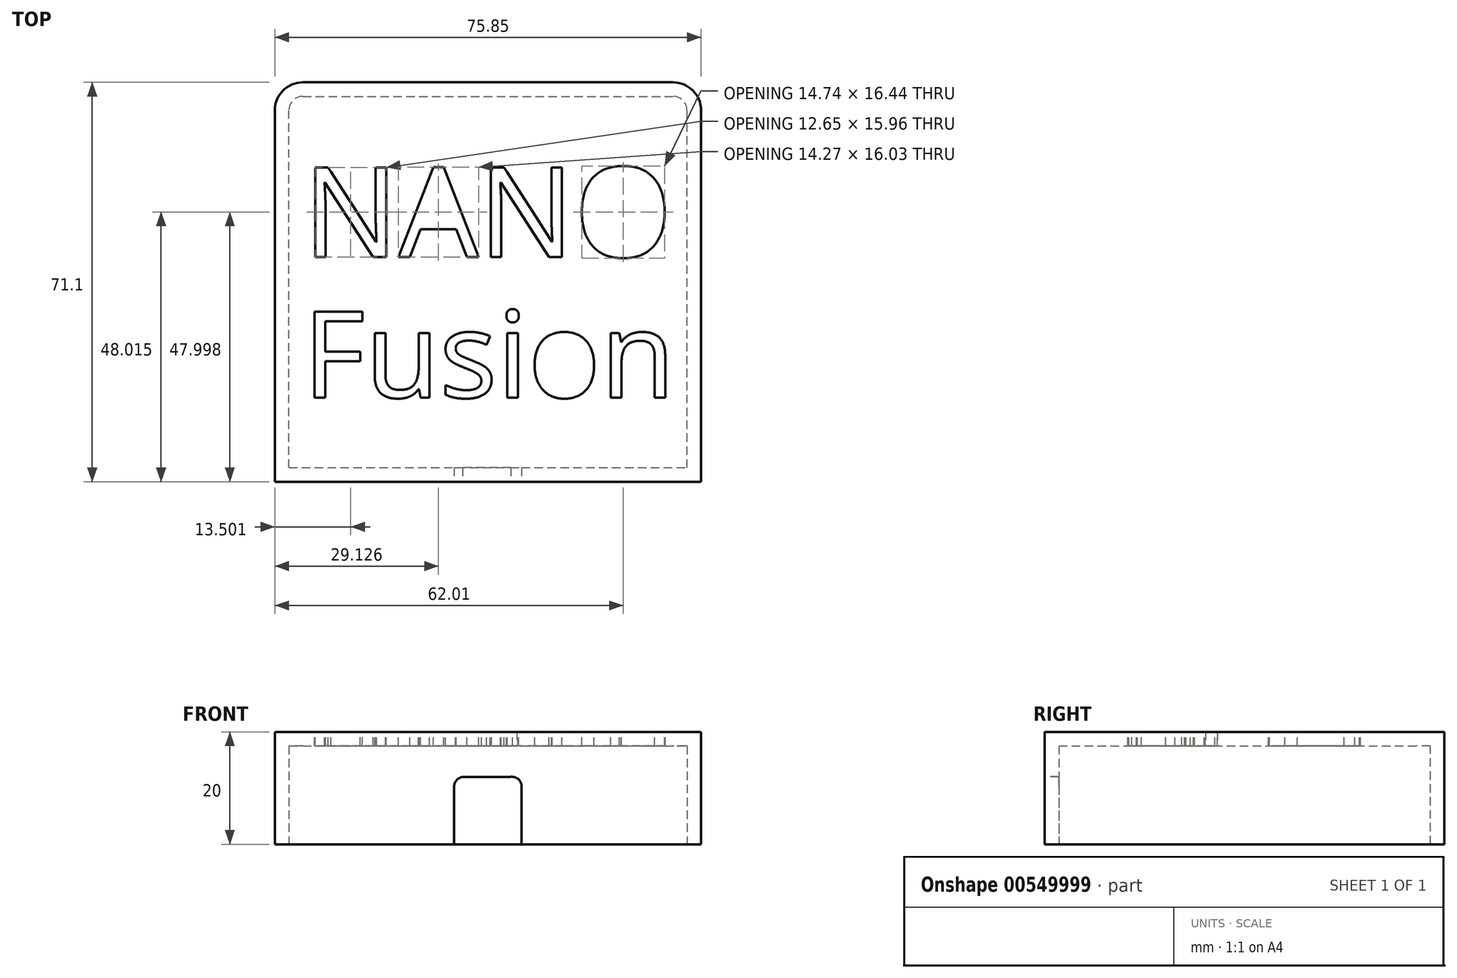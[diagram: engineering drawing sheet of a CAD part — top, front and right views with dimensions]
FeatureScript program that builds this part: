
annotation { "Feature Type Name" : "Feature", "Feature Type Description" : "" }
export const myFeature = defineFeature(function(context is Context, id is Id, definition is map)
    precondition{}
    {
        {
            var Q0;
            Q0=qCreatedBy(makeId("Top.planeOp"),FACE);
            var sketch = newSketch(context, id + "F0", { "sketchPlane" : qUnion([Q0])});
            skLineSegment(sketch, "E0.bottom", {"start": v(0, 0) * mm, "end": v(75.85, 0) * mm});
            skLineSegment(sketch, "E0.top", {"start": v(0, 66.1) * mm, "end": v(75.85, 66.1) * mm, "construction": true});
            skLineSegment(sketch, "E0.left", {"start": v(0, 0) * mm, "end": v(0, 66.1) * mm});
            skLineSegment(sketch, "E0.right", {"start": v(75.85, 0) * mm, "end": v(75.85, 66.1) * mm});
            skArc(sketch, "E1", {"start": v(0, 66.1) * mm, "mid": v(1.46, 69.64) * mm, "end": v(5, 71.1) * mm});
            skLineSegment(sketch, "E2", {"start": v(5, 71.1) * mm, "end": v(70.85, 71.1) * mm});
            skArc(sketch, "E3", {"start": v(70.85, 71.1) * mm, "mid": v(74.39, 69.64) * mm, "end": v(75.85, 66.1) * mm});
            skSolve(sketch);
        }
        {
            var Q0;
            Q0 = qSketchRegion(id + "F0", true);
            extrude(context, id + "F1", {"entities" : qUnion([Q0]), "depth" : 20 * mm, "offsetDistance" : 25 * mm});
        }
        {
            var Q0;
            Q0=makeQuery(id+"F1.opExtrude","CAP_FACE",FACE,{"disambiguationData":[OSD([sQuery(id+"F0.wireOp",EDGE,"E0.bottom"),sQuery(id+"F0.wireOp",EDGE,"E0.left"),sQuery(id+"F0.wireOp",EDGE,"E0.right"),sQuery(id+"F0.wireOp",EDGE,"E1"),sQuery(id+"F0.wireOp",EDGE,"E2"),sQuery(id+"F0.wireOp",EDGE,"E3")])],"isStart":true});
            shell(context, id + "F2", {"entities" : qUnion([Q0]), "thickness" : 2.5 * mm});
        }
        {
            var Q0;
            Q0=makeQuery(id+"F1.opExtrude","CAP_FACE",FACE,{"disambiguationData":[OSD([sQuery(id+"F0.wireOp",EDGE,"E0.bottom"),sQuery(id+"F0.wireOp",EDGE,"E0.left"),sQuery(id+"F0.wireOp",EDGE,"E0.right"),sQuery(id+"F0.wireOp",EDGE,"E1"),sQuery(id+"F0.wireOp",EDGE,"E2"),sQuery(id+"F0.wireOp",EDGE,"E3")])],"isStart":false});
            var sketch = newSketch(context, id + "F3", { "sketchPlane" : qUnion([Q0])});
            skText(sketch, "E4", { "text": "NANO", "fontName": "NotoSans-Regular.ttf"});
            skText(sketch, "E5", { "text": "Fusion", "fontName": "NotoSans-Regular.ttf"});
            const initialGuessF3  = {"E4": [0.005, 0.04, 1, 0, 0.0161], "E5": [0.005, 0.015, 1, 0, 0.01539]};
            skSetInitialGuess(sketch, initialGuessF3);
            skSolve(sketch);
        }
        {
            var Q0;
            Q0 = qSketchRegion(id + "F3", true);
            extrude(context, id + "F4", {"entities" : qUnion([Q0]), "operationType" : NewBodyOperationType.REMOVE, "oppositeDirection" : true, "depth" : 25 * mm, "offsetDistance" : 25 * mm});
        }
        {
            var Q0;
            Q0=makeQuery(id+"F4.boolean.opBoolean","SPLIT",FACE,{"disambiguationData":[TD([makeQuery(id+"F4.opExtrude","SWEPT_FACE",FACE,{"disambiguationData":[OSD([sQuery(id+"F3.wireOp",EDGE,"E4.sketch_text.stroke-26")])]})])],"derivedFrom":makeQuery(id+"F1.opExtrude","CAP_FACE",FACE,{"disambiguationData":[OSD([sQuery(id+"F0.wireOp",EDGE,"E0.bottom"),sQuery(id+"F0.wireOp",EDGE,"E0.left"),sQuery(id+"F0.wireOp",EDGE,"E0.right"),sQuery(id+"F0.wireOp",EDGE,"E1"),sQuery(id+"F0.wireOp",EDGE,"E2"),sQuery(id+"F0.wireOp",EDGE,"E3")])],"isStart":false})});
            extrude(context, id + "F5", {"entities" : qUnion([Q0]), "operationType" : NewBodyOperationType.REMOVE, "oppositeDirection" : true, "depth" : 25 * mm, "offsetDistance" : 25 * mm});
        }
        {
            var Q0;
            Q0=makeQuery(id+"F4.boolean.opBoolean","SPLIT",FACE,{"disambiguationData":[TD([makeQuery(id+"F4.opExtrude","SWEPT_FACE",FACE,{"disambiguationData":[OSD([sQuery(id+"F3.wireOp",EDGE,"E4.sketch_text.stroke-57")])]})])],"derivedFrom":makeQuery(id+"F1.opExtrude","CAP_FACE",FACE,{"disambiguationData":[OSD([sQuery(id+"F0.wireOp",EDGE,"E0.bottom"),sQuery(id+"F0.wireOp",EDGE,"E0.left"),sQuery(id+"F0.wireOp",EDGE,"E0.right"),sQuery(id+"F0.wireOp",EDGE,"E1"),sQuery(id+"F0.wireOp",EDGE,"E2"),sQuery(id+"F0.wireOp",EDGE,"E3")])],"isStart":false})});
            extrude(context, id + "F6", {"entities" : qUnion([Q0]), "operationType" : NewBodyOperationType.REMOVE, "oppositeDirection" : true, "depth" : 25 * mm, "offsetDistance" : 25 * mm});
        }
        {
            var Q0;
            Q0=makeQuery(id+"F4.boolean.opBoolean","SPLIT",FACE,{"disambiguationData":[TD([makeQuery(id+"F4.opExtrude","SWEPT_FACE",FACE,{"disambiguationData":[OSD([sQuery(id+"F3.wireOp",EDGE,"E5.sketch_text.stroke-72")])]})])],"derivedFrom":makeQuery(id+"F1.opExtrude","CAP_FACE",FACE,{"disambiguationData":[OSD([sQuery(id+"F0.wireOp",EDGE,"E0.bottom"),sQuery(id+"F0.wireOp",EDGE,"E0.left"),sQuery(id+"F0.wireOp",EDGE,"E0.right"),sQuery(id+"F0.wireOp",EDGE,"E1"),sQuery(id+"F0.wireOp",EDGE,"E2"),sQuery(id+"F0.wireOp",EDGE,"E3")])],"isStart":false})});
            extrude(context, id + "F7", {"entities" : qUnion([Q0]), "operationType" : NewBodyOperationType.REMOVE, "oppositeDirection" : true, "depth" : 25 * mm, "offsetDistance" : 25 * mm});
        }
        {
            var Q0;
            Q0=makeQuery(id+"F1.opExtrude","SWEPT_FACE",FACE,{"disambiguationData":[OSD([sQuery(id+"F0.wireOp",EDGE,"E0.bottom")])]});
            var sketch = newSketch(context, id + "F8", { "sketchPlane" : qUnion([Q0])});
            skPoint(sketch, "E6", {"position": v(37.92, 0) * mm});
            skLineSegment(sketch, "E7.bottom", {"start": v(31.92, 0) * mm, "end": v(43.93, 0) * mm});
            skLineSegment(sketch, "E7.top", {"start": v(31.92, 10.27) * mm, "end": v(43.93, 10.27) * mm, "construction": true});
            skLineSegment(sketch, "E7.left", {"start": v(31.92, 0) * mm, "end": v(31.92, 10.27) * mm});
            skLineSegment(sketch, "E7.right", {"start": v(43.92, 0) * mm, "end": v(43.92, 10.27) * mm});
            skArc(sketch, "E8", {"start": v(31.92, 10.27) * mm, "mid": v(32.36, 11.43) * mm, "end": v(33.45, 12) * mm});
            skArc(sketch, "E9", {"start": v(43.93, 10.27) * mm, "mid": v(43.34, 11.58) * mm, "end": v(41.98, 12) * mm});
            skLineSegment(sketch, "E10", {"start": v(33.45, 12) * mm, "end": v(41.98, 12) * mm});
            skSolve(sketch);
        }
        {
            var Q0;
            Q0 = qSketchRegion(id + "F8", true);
            extrude(context, id + "F9", {"entities" : qUnion([Q0]), "operationType" : NewBodyOperationType.REMOVE, "oppositeDirection" : true, "depth" : 25 * mm, "offsetDistance" : 25 * mm});
        }
    });
